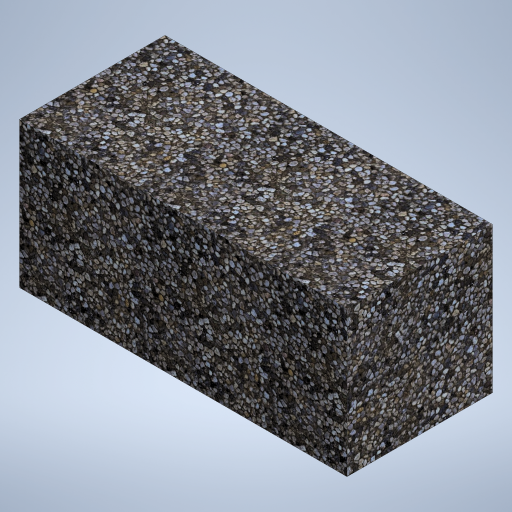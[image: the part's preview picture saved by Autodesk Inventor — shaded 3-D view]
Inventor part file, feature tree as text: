
AUTODESK INVENTOR PART (.ipt)
format: ipt  version: 2023 (Build 270158000, 158)  size: 574,464 bytes
history: native  units: in
note: dims shown in document units (in); Inventor stores cm internally (conversion verified against a paired STEP export)
features: extrude x1, shell x1, sketch x1
ambient origin geometry x8: Origin, YZ Plane, XZ Plane, XY Plane, X Axis, Y Axis, Z Axis, Center Point
bodies: Solid1 (feature_tree)
feature tree (3):
  extrude  "Extrusion1"  Depth=8.0in
  shell  "Shell1"  Thickness=18.0in
  sketch  "Sketch1"  dims[d0=8.0in d1=8.0in d2=18.0in d3=0.0in d4=0.34in]
